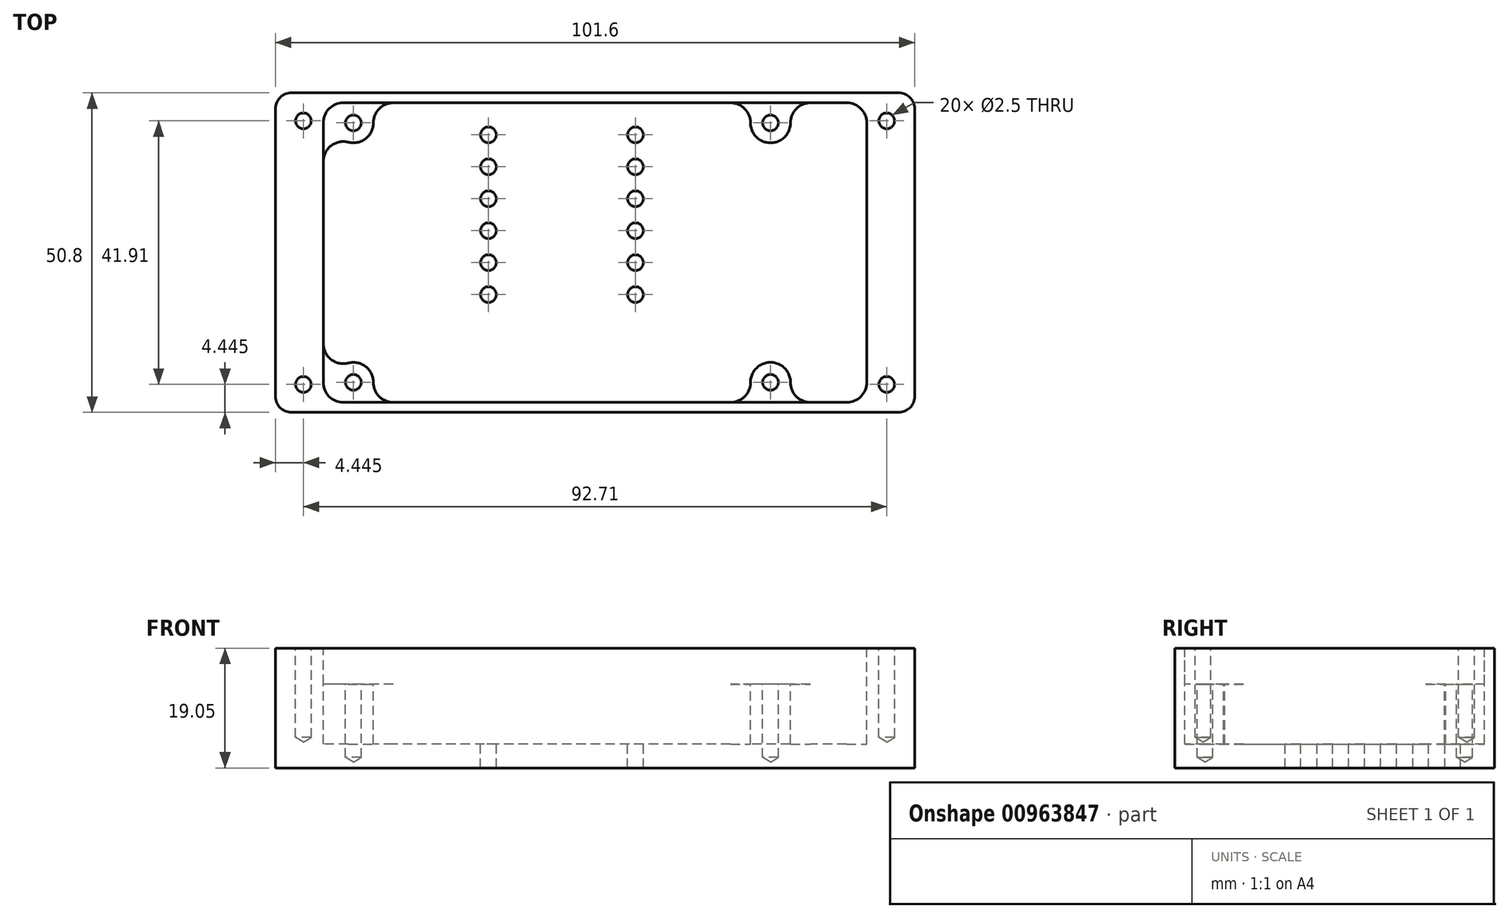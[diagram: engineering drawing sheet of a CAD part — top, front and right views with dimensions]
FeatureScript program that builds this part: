
annotation { "Feature Type Name" : "Feature", "Feature Type Description" : "" }
export const myFeature = defineFeature(function(context is Context, id is Id, definition is map)
    precondition{}
    {
        {
            var Q0;
            Q0=qCreatedBy(makeId("Top.planeOp"),FACE);
            var sketch = newSketch(context, id + "F0", { "sketchPlane" : qUnion([Q0])});
            skLineSegment(sketch, "E0.bottom", {"start": v(50.8, -25.4) * mm, "end": v(-50.8, -25.4) * mm});
            skLineSegment(sketch, "E0.top", {"start": v(50.8, 25.4) * mm, "end": v(-50.8, 25.4) * mm});
            skLineSegment(sketch, "E0.left", {"start": v(50.8, -25.4) * mm, "end": v(50.8, 25.4) * mm});
            skLineSegment(sketch, "E0.right", {"start": v(-50.8, -25.4) * mm, "end": v(-50.8, 25.4) * mm});
            skPoint(sketch, "E0.middle", {"position": v(0, 0) * mm});
            skSolve(sketch);
        }
        {
            var Q0;
            Q0=makeQuery(id+"F0.imprint","IMPRINT",FACE,{"disambiguationData":[TD([[makeQuery(id+"F0.imprint","IMPRINT",EDGE,{"derivedFrom":sQuery(id+"F0.wireOp",EDGE,"E0.bottom")}),-1.0]])]});
            extrude(context, id + "F1", {"entities" : qUnion([Q0]), "oppositeDirection" : true, "depth" : 19.05 * mm, "offsetDistance" : 25.4 * mm});
        }
        {
            var Q0;
            Q0=makeQuery(id+"F1.opExtrude","SWEPT_EDGE",EDGE,{"disambiguationData":[OSD([sQuery(id+"F0.wireOp",EDGE,"E0.bottom"),sQuery(id+"F0.wireOp",EDGE,"E0.right")])]});
            var Q1;
            Q1=makeQuery(id+"F1.opExtrude","SWEPT_EDGE",EDGE,{"disambiguationData":[OSD([sQuery(id+"F0.wireOp",EDGE,"E0.bottom"),sQuery(id+"F0.wireOp",EDGE,"E0.left")])]});
            var Q2;
            Q2=makeQuery(id+"F1.opExtrude","SWEPT_EDGE",EDGE,{"disambiguationData":[OSD([sQuery(id+"F0.wireOp",EDGE,"E0.top"),sQuery(id+"F0.wireOp",EDGE,"E0.left")])]});
            var Q3;
            Q3=makeQuery(id+"F1.opExtrude","SWEPT_EDGE",EDGE,{"disambiguationData":[OSD([sQuery(id+"F0.wireOp",EDGE,"E0.top"),sQuery(id+"F0.wireOp",EDGE,"E0.right")])]});
            fillet(context, id + "F2", {"entities" : qUnion([Q0, Q1, Q2, Q3]), "radius" : 2.54 * mm, "tangentPropagation" : true, "allowEdgeOverflow" : false});
        }
        {
            var Q0;
            Q0=makeQuery(id+"F1.opExtrude","CAP_FACE",FACE,{"disambiguationData":[OSD([sQuery(id+"F0.wireOp",EDGE,"E0.bottom"),sQuery(id+"F0.wireOp",EDGE,"E0.top"),sQuery(id+"F0.wireOp",EDGE,"E0.left"),sQuery(id+"F0.wireOp",EDGE,"E0.right")])],"isStart":true});
            var sketch = newSketch(context, id + "F3", { "sketchPlane" : qUnion([Q0])});
            skPoint(sketch, "E1", {"position": v(-46.36, 20.95) * mm});
            skPoint(sketch, "E2", {"position": v(46.36, 20.95) * mm});
            skPoint(sketch, "E3", {"position": v(46.36, -20.96) * mm});
            skPoint(sketch, "E4", {"position": v(-46.36, -20.96) * mm});
            skSolve(sketch);
        }
        {
            var Q0;
            Q0=sQuery(id+"F3.wireOp",VERTEX,"E1");
            var Q1;
            Q1=sQuery(id+"F3.wireOp",VERTEX,"E2");
            var Q2;
            Q2=sQuery(id+"F3.wireOp",VERTEX,"E3");
            var Q3;
            Q3=sQuery(id+"F3.wireOp",VERTEX,"E4");
            var Q4;
            Q4=makeQuery(id+"F1.opExtrude","SWEPT_BODY",BODY,{"disambiguationData":[OSD([sQuery(id+"F0.wireOp",EDGE,"E0.bottom"),sQuery(id+"F0.wireOp",EDGE,"E0.top"),sQuery(id+"F0.wireOp",EDGE,"E0.left"),sQuery(id+"F0.wireOp",EDGE,"E0.right")])]});
            hole(context, id + "F4", {"style" : HoleStyle.SIMPLE, "endStyle" : HoleEndStyle.BLIND, "standardTappedOrClearance" : lookupTablePath({ "standard" : "ISO", "engagement" : "75%", "pitch" : "0.5 mm", "size" : "M3", "type" : "Tapped" }), "standardBlindInLast" : lookupTablePath({ "standard" : "ISO", "fit" : "Normal", "engagement" : "75%", "pitch" : "0.5 mm", "size" : "M3", "type" : "Clearance & tapped" }), "holeDiameter" : 2.5 * mm, "majorDiameter" : 3 * mm, "showTappedDepth" : true, "holeDepth" : 14.2 * mm, "isTappedThrough" : true, "tappedDepth" : 12.7 * mm, "tapClearance" : 3, "startFromSketch" : true, "locations" : qUnion([Q0, Q1, Q2, Q3]), "scope" : qUnion([Q4])});
        }
        {
            var Q0;
            Q0=makeQuery(id+"F1.opExtrude","CAP_FACE",FACE,{"disambiguationData":[OSD([sQuery(id+"F0.wireOp",EDGE,"E0.bottom"),sQuery(id+"F0.wireOp",EDGE,"E0.top"),sQuery(id+"F0.wireOp",EDGE,"E0.left"),sQuery(id+"F0.wireOp",EDGE,"E0.right")])],"isStart":true});
            var sketch = newSketch(context, id + "F5", { "sketchPlane" : qUnion([Q0])});
            skLineSegment(sketch, "E5.bottom", {"start": v(40, -23.81) * mm, "end": v(-40, -23.81) * mm});
            skLineSegment(sketch, "E5.top", {"start": v(40, 23.81) * mm, "end": v(-40, 23.81) * mm});
            skLineSegment(sketch, "E5.left", {"start": v(43.18, -20.64) * mm, "end": v(43.18, 20.64) * mm});
            skLineSegment(sketch, "E5.right", {"start": v(-43.18, -20.64) * mm, "end": v(-43.18, 20.64) * mm});
            skPoint(sketch, "E5.middle", {"position": v(0, 0) * mm});
            skPoint(sketch, "E6.visualSharp", {"position": v(-43.18, 23.81) * mm});
            skArc(sketch, "E6.filletArc", {"start": v(-40, 23.81) * mm, "mid": v(-42.25, 22.88) * mm, "end": v(-43.18, 20.64) * mm});
            skPoint(sketch, "E7.visualSharp", {"position": v(-43.18, -23.81) * mm});
            skArc(sketch, "E7.filletArc", {"start": v(-43.18, -20.64) * mm, "mid": v(-42.25, -22.88) * mm, "end": v(-40, -23.81) * mm});
            skPoint(sketch, "E8.visualSharp", {"position": v(43.18, -23.81) * mm});
            skArc(sketch, "E8.filletArc", {"start": v(40, -23.81) * mm, "mid": v(42.25, -22.88) * mm, "end": v(43.18, -20.64) * mm});
            skPoint(sketch, "E9.visualSharp", {"position": v(43.18, 23.81) * mm});
            skArc(sketch, "E9.filletArc", {"start": v(43.18, 20.64) * mm, "mid": v(42.25, 22.88) * mm, "end": v(40, 23.81) * mm});
            skSolve(sketch);
        }
        {
            var Q0;
            Q0 = qSketchRegion(id + "F5", true);
            extrude(context, id + "F6", {"entities" : qUnion([Q0]), "operationType" : NewBodyOperationType.REMOVE, "oppositeDirection" : true, "depth" : 5.7 * mm, "offsetDistance" : 25.4 * mm});
        }
        {
            var Q0;
            Q0=makeQuery(id+"F6.boolean.opBoolean","COPY",FACE,{"derivedFrom":makeQuery(id+"F6.opExtrude","CAP_FACE",FACE,{"disambiguationData":[OSD([sQuery(id+"F5.wireOp",EDGE,"E5.bottom"),sQuery(id+"F5.wireOp",EDGE,"E5.top"),sQuery(id+"F5.wireOp",EDGE,"E5.left"),sQuery(id+"F5.wireOp",EDGE,"E5.right"),sQuery(id+"F5.wireOp",EDGE,"E6.filletArc"),sQuery(id+"F5.wireOp",EDGE,"E7.filletArc"),sQuery(id+"F5.wireOp",EDGE,"E8.filletArc"),sQuery(id+"F5.wireOp",EDGE,"E9.filletArc")])],"isStart":false})});
            var sketch = newSketch(context, id + "F7", { "sketchPlane" : qUnion([Q0])});
            skPoint(sketch, "E10", {"position": v(-38.4, 20.62) * mm});
            skPoint(sketch, "E11", {"position": v(27.89, 20.62) * mm});
            skPoint(sketch, "E12", {"position": v(27.89, -20.62) * mm});
            skPoint(sketch, "E13", {"position": v(-38.4, -20.62) * mm});
            skSolve(sketch);
        }
        {
            var Q0;
            Q0=sQuery(id+"F7.wireOp",VERTEX,"E10");
            var Q1;
            Q1=sQuery(id+"F7.wireOp",VERTEX,"E11");
            var Q2;
            Q2=sQuery(id+"F7.wireOp",VERTEX,"E12");
            var Q3;
            Q3=sQuery(id+"F7.wireOp",VERTEX,"E13");
            var Q4;
            Q4=makeQuery(id+"F1.opExtrude","SWEPT_BODY",BODY,{"disambiguationData":[OSD([sQuery(id+"F0.wireOp",EDGE,"E0.bottom"),sQuery(id+"F0.wireOp",EDGE,"E0.top"),sQuery(id+"F0.wireOp",EDGE,"E0.left"),sQuery(id+"F0.wireOp",EDGE,"E0.right")])]});
            hole(context, id + "F8", {"style" : HoleStyle.SIMPLE, "endStyle" : HoleEndStyle.BLIND, "standardTappedOrClearance" : lookupTablePath({ "standard" : "ISO", "engagement" : "75%", "pitch" : "0.5 mm", "size" : "M3", "type" : "Tapped" }), "standardBlindInLast" : lookupTablePath({ "standard" : "ISO", "fit" : "Normal", "engagement" : "75%", "pitch" : "0.5 mm", "size" : "M3", "type" : "Clearance & tapped" }), "holeDiameter" : 2.5 * mm, "majorDiameter" : 3 * mm, "showTappedDepth" : true, "holeDepth" : 11.66 * mm, "isTappedThrough" : true, "tappedDepth" : 10.16 * mm, "tapClearance" : 3, "startFromSketch" : true, "locations" : qUnion([Q0, Q1, Q2, Q3]), "scope" : qUnion([Q4])});
        }
        {
            var Q0;
            Q0=makeQuery(id+"F6.boolean.opBoolean","COPY",FACE,{"derivedFrom":makeQuery(id+"F6.opExtrude","CAP_FACE",FACE,{"disambiguationData":[OSD([sQuery(id+"F5.wireOp",EDGE,"E5.bottom"),sQuery(id+"F5.wireOp",EDGE,"E5.top"),sQuery(id+"F5.wireOp",EDGE,"E5.left"),sQuery(id+"F5.wireOp",EDGE,"E5.right"),sQuery(id+"F5.wireOp",EDGE,"E6.filletArc"),sQuery(id+"F5.wireOp",EDGE,"E7.filletArc"),sQuery(id+"F5.wireOp",EDGE,"E8.filletArc"),sQuery(id+"F5.wireOp",EDGE,"E9.filletArc")])],"isStart":false})});
            var sketch = newSketch(context, id + "F9", { "sketchPlane" : qUnion([Q0])});
            skLineSegment(sketch, "E14.bottom", {"start": v(40, -23.81) * mm, "end": v(34.24, -23.81) * mm});
            skLineSegment(sketch, "E14.top", {"start": v(40, 23.81) * mm, "end": v(34.24, 23.81) * mm});
            skLineSegment(sketch, "E14.left", {"start": v(43.18, -20.64) * mm, "end": v(43.18, 20.64) * mm});
            skLineSegment(sketch, "E14.right", {"start": v(-43.18, -14.48) * mm, "end": v(-43.18, 14.48) * mm});
            skPoint(sketch, "E14.middle", {"position": v(0, 0) * mm});
            skArc(sketch, "E15", {"start": v(-39.2, 17.55) * mm, "mid": v(-36.46, 18.11) * mm, "end": v(-35.23, 20.63) * mm});
            skArc(sketch, "E16", {"start": v(-32.05, 23.81) * mm, "mid": v(-34.3, 22.88) * mm, "end": v(-35.23, 20.63) * mm});
            skArc(sketch, "E17", {"start": v(-39.2, 17.55) * mm, "mid": v(-41.95, 17) * mm, "end": v(-43.18, 14.48) * mm});
            skPoint(sketch, "E18.orphan", {"position": v(-43.18, 23.81) * mm});
            skArc(sketch, "E19", {"start": v(24.71, 20.63) * mm, "mid": v(27.89, 17.45) * mm, "end": v(31.06, 20.63) * mm});
            skArc(sketch, "E20", {"start": v(34.24, 23.81) * mm, "mid": v(32, 22.88) * mm, "end": v(31.06, 20.63) * mm});
            skArc(sketch, "E21", {"start": v(24.71, 20.63) * mm, "mid": v(23.79, 22.88) * mm, "end": v(21.54, 23.81) * mm});
            skLineSegment(sketch, "E22.trimOffspring", {"start": v(21.54, 23.81) * mm, "end": v(-32.05, 23.81) * mm});
            skPoint(sketch, "E23.visualSharp", {"position": v(43.18, 23.81) * mm});
            skArc(sketch, "E23.filletArc", {"start": v(43.18, 20.64) * mm, "mid": v(42.25, 22.88) * mm, "end": v(40, 23.81) * mm});
            skArc(sketch, "E24.MirrorCS", {"start": v(-39.2, -17.55) * mm, "mid": v(-41.95, -17) * mm, "end": v(-43.18, -14.48) * mm});
            skArc(sketch, "E25.MirrorCS", {"start": v(-39.2, -17.55) * mm, "mid": v(-36.46, -18.11) * mm, "end": v(-35.23, -20.63) * mm});
            skArc(sketch, "E26.MirrorCS", {"start": v(-32.05, -23.81) * mm, "mid": v(-34.3, -22.88) * mm, "end": v(-35.23, -20.63) * mm});
            skArc(sketch, "E27.MirrorCS", {"start": v(24.71, -20.63) * mm, "mid": v(23.79, -22.88) * mm, "end": v(21.54, -23.81) * mm});
            skArc(sketch, "E28.MirrorCS", {"start": v(24.71, -20.63) * mm, "mid": v(27.89, -17.45) * mm, "end": v(31.06, -20.63) * mm});
            skArc(sketch, "E29.MirrorCS", {"start": v(34.24, -23.81) * mm, "mid": v(32, -22.88) * mm, "end": v(31.06, -20.63) * mm});
            skArc(sketch, "E30.MirrorCS", {"start": v(43.18, -20.64) * mm, "mid": v(42.25, -22.88) * mm, "end": v(40, -23.81) * mm});
            skPoint(sketch, "E31.orphan", {"position": v(-43.18, -23.81) * mm});
            skLineSegment(sketch, "E32.trimOffspring", {"start": v(21.54, -23.81) * mm, "end": v(-32.05, -23.81) * mm});
            skPoint(sketch, "E33.orphan", {"position": v(43.18, -23.81) * mm});
            skSolve(sketch);
        }
        {
            var Q0;
            Q0 = qSketchRegion(id + "F9", true);
            extrude(context, id + "F10", {"entities" : qUnion([Q0]), "operationType" : NewBodyOperationType.REMOVE, "oppositeDirection" : true, "depth" : 9.52 * mm, "offsetDistance" : 25.4 * mm});
        }
        {
            var Q0;
            Q0=makeQuery(id+"F10.boolean.opBoolean","COPY",FACE,{"derivedFrom":makeQuery(id+"F10.opExtrude","CAP_FACE",FACE,{"disambiguationData":[OSD([sQuery(id+"F9.wireOp",EDGE,"E14.bottom"),sQuery(id+"F9.wireOp",EDGE,"E14.top"),sQuery(id+"F9.wireOp",EDGE,"E14.left"),sQuery(id+"F9.wireOp",EDGE,"E14.right"),sQuery(id+"F9.wireOp",EDGE,"E15"),sQuery(id+"F9.wireOp",EDGE,"E16"),sQuery(id+"F9.wireOp",EDGE,"E17"),sQuery(id+"F9.wireOp",EDGE,"E19"),sQuery(id+"F9.wireOp",EDGE,"E20"),sQuery(id+"F9.wireOp",EDGE,"E21"),sQuery(id+"F9.wireOp",EDGE,"E22.trimOffspring"),sQuery(id+"F9.wireOp",EDGE,"E23.filletArc"),sQuery(id+"F9.wireOp",EDGE,"E24.MirrorCS"),sQuery(id+"F9.wireOp",EDGE,"E25.MirrorCS"),sQuery(id+"F9.wireOp",EDGE,"E26.MirrorCS"),sQuery(id+"F9.wireOp",EDGE,"E27.MirrorCS"),sQuery(id+"F9.wireOp",EDGE,"E28.MirrorCS"),sQuery(id+"F9.wireOp",EDGE,"E29.MirrorCS"),sQuery(id+"F9.wireOp",EDGE,"E30.MirrorCS"),sQuery(id+"F9.wireOp",EDGE,"E32.trimOffspring")])],"isStart":false})});
            var sketch = newSketch(context, id + "F11", { "sketchPlane" : qUnion([Q0])});
            skPoint(sketch, "E34", {"position": v(-16.94, 18.73) * mm});
            skPoint(sketch, "E35", {"position": v(-16.94, 13.65) * mm});
            skPoint(sketch, "E36", {"position": v(-16.94, 8.57) * mm});
            skPoint(sketch, "E37", {"position": v(-16.94, 3.5) * mm});
            skPoint(sketch, "E38", {"position": v(-16.94, -1.59) * mm});
            skPoint(sketch, "E39", {"position": v(-16.94, -6.67) * mm});
            skPoint(sketch, "E40", {"position": v(6.43, 18.73) * mm});
            skPoint(sketch, "E41", {"position": v(6.43, 13.65) * mm});
            skPoint(sketch, "E42", {"position": v(6.43, 8.57) * mm});
            skPoint(sketch, "E43", {"position": v(6.43, 3.5) * mm});
            skPoint(sketch, "E44", {"position": v(6.43, -1.59) * mm});
            skPoint(sketch, "E45", {"position": v(6.43, -6.67) * mm});
            skSolve(sketch);
        }
        {
            var Q0;
            Q0=sQuery(id+"F11.wireOp",VERTEX,"E34");
            var Q1;
            Q1=sQuery(id+"F11.wireOp",VERTEX,"E35");
            var Q2;
            Q2=sQuery(id+"F11.wireOp",VERTEX,"E36");
            var Q3;
            Q3=sQuery(id+"F11.wireOp",VERTEX,"E37");
            var Q4;
            Q4=sQuery(id+"F11.wireOp",VERTEX,"E38");
            var Q5;
            Q5=sQuery(id+"F11.wireOp",VERTEX,"E39");
            var Q6;
            Q6=sQuery(id+"F11.wireOp",VERTEX,"E45");
            var Q7;
            Q7=sQuery(id+"F11.wireOp",VERTEX,"E44");
            var Q8;
            Q8=sQuery(id+"F11.wireOp",VERTEX,"E43");
            var Q9;
            Q9=sQuery(id+"F11.wireOp",VERTEX,"E42");
            var Q10;
            Q10=sQuery(id+"F11.wireOp",VERTEX,"E41");
            var Q11;
            Q11=sQuery(id+"F11.wireOp",VERTEX,"E40");
            var Q12;
            Q12=makeQuery(id+"F1.opExtrude","SWEPT_BODY",BODY,{"disambiguationData":[OSD([sQuery(id+"F0.wireOp",EDGE,"E0.bottom"),sQuery(id+"F0.wireOp",EDGE,"E0.top"),sQuery(id+"F0.wireOp",EDGE,"E0.left"),sQuery(id+"F0.wireOp",EDGE,"E0.right")])]});
            hole(context, id + "F12", {"style" : HoleStyle.SIMPLE, "endStyle" : HoleEndStyle.BLIND, "holeDiameter" : 2.5 * mm, "majorDiameter" : 3 * mm, "holeDepth" : 3.8 * mm, "isTappedThrough" : true, "tappedDepth" : 12.7 * mm, "tapClearance" : 3, "startFromSketch" : true, "locations" : qUnion([Q0, Q1, Q2, Q3, Q4, Q5, Q6, Q7, Q8, Q9, Q10, Q11]), "scope" : qUnion([Q12])});
        }
    });
